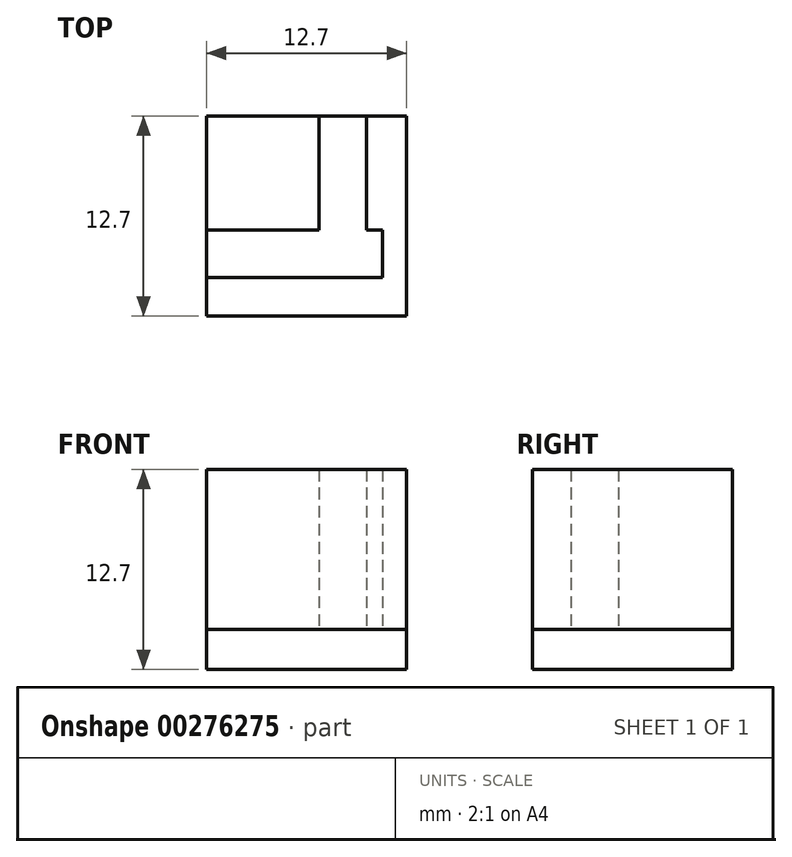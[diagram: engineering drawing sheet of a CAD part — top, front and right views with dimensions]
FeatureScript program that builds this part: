
annotation { "Feature Type Name" : "Feature", "Feature Type Description" : "" }
export const myFeature = defineFeature(function(context is Context, id is Id, definition is map)
    precondition{}
    {
        {
            var Q0;
            Q0=qCreatedBy(makeId("Top.planeOp"),FACE);
            var sketch = newSketch(context, id + "F0", { "sketchPlane" : qUnion([Q0])});
            skLineSegment(sketch, "E0.bottom", {"start": v(-14.96, 0.92) * mm, "end": v(-2.26, 0.92) * mm});
            skLineSegment(sketch, "E0.top", {"start": v(-14.96, -11.78) * mm, "end": v(-2.26, -11.78) * mm});
            skLineSegment(sketch, "E0.left", {"start": v(-14.96, 0.92) * mm, "end": v(-14.96, -11.78) * mm});
            skLineSegment(sketch, "E0.right", {"start": v(-2.26, 0.92) * mm, "end": v(-2.26, -11.78) * mm});
            skLineSegment(sketch, "E1.bottom", {"start": v(-12.42, 0.92) * mm, "end": v(-9.42, 0.92) * mm});
            skLineSegment(sketch, "E1.top", {"start": v(-12.42, -9.32) * mm, "end": v(-9.42, -9.32) * mm});
            skLineSegment(sketch, "E1.left", {"start": v(-12.42, 0.92) * mm, "end": v(-12.42, -6.32) * mm});
            skLineSegment(sketch, "E1.right", {"start": v(-9.42, 0.92) * mm, "end": v(-9.42, -6.32) * mm});
            skLineSegment(sketch, "E2.bottom", {"start": v(-13.44, -6.32) * mm, "end": v(-12.42, -6.32) * mm});
            skLineSegment(sketch, "E2.top", {"start": v(-13.44, -9.32) * mm, "end": v(-2.26, -9.32) * mm});
            skLineSegment(sketch, "E2.left", {"start": v(-13.44, -6.32) * mm, "end": v(-13.44, -9.32) * mm});
            skLineSegment(sketch, "E2.right", {"start": v(-2.26, -6.32) * mm, "end": v(-2.26, -9.32) * mm});
            skLineSegment(sketch, "E3.trimOffspring", {"start": v(-9.42, -6.32) * mm, "end": v(-2.26, -6.32) * mm});
            skSolve(sketch);
        }
        {
            var Q0;
            {var subQ3=sQuery(id+"F0.wireOp",EDGE,"E1.right");Q0=makeQuery(id+"F0.imprint","IMPRINT",FACE,{"disambiguationData":[TD([[makeQuery(id+"F0.imprint","IMPRINT",EDGE,{"derivedFrom":subQ3}),1.0]])]});}
            var Q1;
            {var subQ1=sQuery(id+"F0.wireOp",EDGE,"E0.top");Q1=makeQuery(id+"F0.imprint","IMPRINT",FACE,{"disambiguationData":[TD([[makeQuery(id+"F0.imprint","IMPRINT",EDGE,{"derivedFrom":subQ1}),1.0]])]});}
            extrude(context, id + "F1", {"entities" : qUnion([Q0, Q1]), "depth" : 10.16 * mm});
        }
        {
            var Q0;
            Q0=makeQuery(id+"F1.opExtrude","CAP_FACE",FACE,{"disambiguationData":[OSD([sQuery(id+"F0.wireOp",EDGE,"E0.bottom"),sQuery(id+"F0.wireOp",EDGE,"E0.right"),sQuery(id+"F0.wireOp",EDGE,"E1.right"),sQuery(id+"F0.wireOp",EDGE,"E3.trimOffspring")])],"isStart":true});
            var sketch = newSketch(context, id + "F2", { "sketchPlane" : qUnion([Q0])});
            skLineSegment(sketch, "E4.0.0", {"start": v(-13.44, 9.32) * mm, "end": v(-2.26, 9.32) * mm});
            skLineSegment(sketch, "E4.0.1", {"start": v(-2.26, 9.32) * mm, "end": v(-2.26, 11.78) * mm});
            skLineSegment(sketch, "E4.0.2", {"start": v(-2.26, 11.78) * mm, "end": v(-14.96, 11.78) * mm});
            skLineSegment(sketch, "E4.0.3", {"start": v(-14.96, 11.78) * mm, "end": v(-14.96, -0.92) * mm});
            skLineSegment(sketch, "E4.0.4", {"start": v(-14.96, -0.92) * mm, "end": v(-12.42, -0.92) * mm});
            skLineSegment(sketch, "E4.0.5", {"start": v(-12.42, -0.92) * mm, "end": v(-12.42, 6.32) * mm});
            skLineSegment(sketch, "E4.0.6", {"start": v(-12.42, 6.32) * mm, "end": v(-13.44, 6.32) * mm});
            skLineSegment(sketch, "E4.0.7", {"start": v(-13.44, 6.32) * mm, "end": v(-13.44, 9.32) * mm});
            skLineSegment(sketch, "E5.0.0", {"start": v(-9.42, 6.32) * mm, "end": v(-9.42, -0.92) * mm});
            skLineSegment(sketch, "E5.0.1", {"start": v(-9.42, -0.92) * mm, "end": v(-2.26, -0.92) * mm});
            skLineSegment(sketch, "E5.0.2", {"start": v(-2.26, -0.92) * mm, "end": v(-2.26, 6.32) * mm});
            skLineSegment(sketch, "E5.0.3", {"start": v(-2.26, 6.32) * mm, "end": v(-9.42, 6.32) * mm});
            skLineSegment(sketch, "E6.bottom", {"start": v(-2.26, -0.92) * mm, "end": v(-14.96, -0.92) * mm});
            skLineSegment(sketch, "E6.left", {"start": v(-2.26, -0.92) * mm, "end": v(-2.26, 11.78) * mm});
            skLineSegment(sketch, "E6.right", {"start": v(-14.96, -0.92) * mm, "end": v(-14.96, 11.78) * mm});
            skSolve(sketch);
        }
        {
            var Q0;
            {var subQ0=sQuery(id+"F2.wireOp",EDGE,"E5.0.0");Q0=makeQuery(id+"F2.imprint","IMPRINT",FACE,{"disambiguationData":[TD([[makeQuery(id+"F2.imprint","IMPRINT",EDGE,{"derivedFrom":subQ0}),-1.0]])]});}
            var Q1;
            {var subQ1=sQuery(id+"F2.wireOp",EDGE,"E4.0.0");Q1=makeQuery(id+"F2.imprint","IMPRINT",FACE,{"disambiguationData":[TD([[makeQuery(id+"F2.imprint","IMPRINT",EDGE,{"derivedFrom":subQ1}),-1.0]])]});}
            var Q2;
            {var subQ2=sQuery(id+"F2.wireOp",EDGE,"E4.0.0");Q2=makeQuery(id+"F2.imprint","IMPRINT",FACE,{"disambiguationData":[TD([[makeQuery(id+"F2.imprint","IMPRINT",EDGE,{"derivedFrom":subQ2}),1.0]])]});}
            extrude(context, id + "F3", {"entities" : qUnion([Q0, Q1, Q2]), "depth" : 2.54 * mm});
        }
        {
            var Q0;
            Q0=makeQuery(id+"F3.opExtrude","SWEPT_FACE",FACE,{"disambiguationData":[OSD([sQuery(id+"F2.wireOp",EDGE,"E6.left")])]});
            cPlane(context, id + "F4", {"entities" : qUnion([Q0]), "cplaneType" : CPlaneType.OFFSET, "offset" : 6.35 * mm, "oppositeDirection" : true, "width" : 152.4 * mm, "height" : 152.4 * mm});
        }
        {
            var Q0;
            Q0=makeQuery(id+"F1.opExtrude","SWEPT_BODY",BODY,{"disambiguationData":[OSD([sQuery(id+"F0.wireOp",EDGE,"E0.bottom"),sQuery(id+"F0.wireOp",EDGE,"E0.right"),sQuery(id+"F0.wireOp",EDGE,"E1.right"),sQuery(id+"F0.wireOp",EDGE,"E3.trimOffspring")])]});
            var Q1;
            Q1=qCreatedBy(id+"F4.planeOp",FACE);
            mirror(context, id + "F5", {"entities" : qUnion([Q0]), "mirrorPlane" : qUnion([Q1])});
        }
        {
            var Q0;
            Q0=makeQuery(id+"F1.opExtrude","SWEPT_BODY",BODY,{"disambiguationData":[OSD([sQuery(id+"F0.wireOp",EDGE,"E0.bottom"),sQuery(id+"F0.wireOp",EDGE,"E0.right"),sQuery(id+"F0.wireOp",EDGE,"E1.right"),sQuery(id+"F0.wireOp",EDGE,"E3.trimOffspring")])]});
            deleteBodies(context, id + "F6", {"entities" : qUnion([Q0])});
        }
        {
            var Q0;
            Q0=makeQuery(id+"F1.opExtrude","SWEPT_BODY",BODY,{"disambiguationData":[OSD([sQuery(id+"F0.wireOp",EDGE,"E0.bottom"),sQuery(id+"F0.wireOp",EDGE,"E0.top"),sQuery(id+"F0.wireOp",EDGE,"E0.left"),sQuery(id+"F0.wireOp",EDGE,"E0.right"),sQuery(id+"F0.wireOp",EDGE,"E1.left"),sQuery(id+"F0.wireOp",EDGE,"E2.bottom"),sQuery(id+"F0.wireOp",EDGE,"E2.top"),sQuery(id+"F0.wireOp",EDGE,"E2.left")])]});
            var Q1;
            Q1=qCreatedBy(id+"F4.planeOp",FACE);
            mirror(context, id + "F7", {"entities" : qUnion([Q0]), "mirrorPlane" : qUnion([Q1])});
        }
        {
            var Q0;
            Q0=makeQuery(id+"F1.opExtrude","SWEPT_BODY",BODY,{"disambiguationData":[OSD([sQuery(id+"F0.wireOp",EDGE,"E0.bottom"),sQuery(id+"F0.wireOp",EDGE,"E0.top"),sQuery(id+"F0.wireOp",EDGE,"E0.left"),sQuery(id+"F0.wireOp",EDGE,"E0.right"),sQuery(id+"F0.wireOp",EDGE,"E1.left"),sQuery(id+"F0.wireOp",EDGE,"E2.bottom"),sQuery(id+"F0.wireOp",EDGE,"E2.top"),sQuery(id+"F0.wireOp",EDGE,"E2.left")])]});
            deleteBodies(context, id + "F8", {"entities" : qUnion([Q0])});
        }
    });
